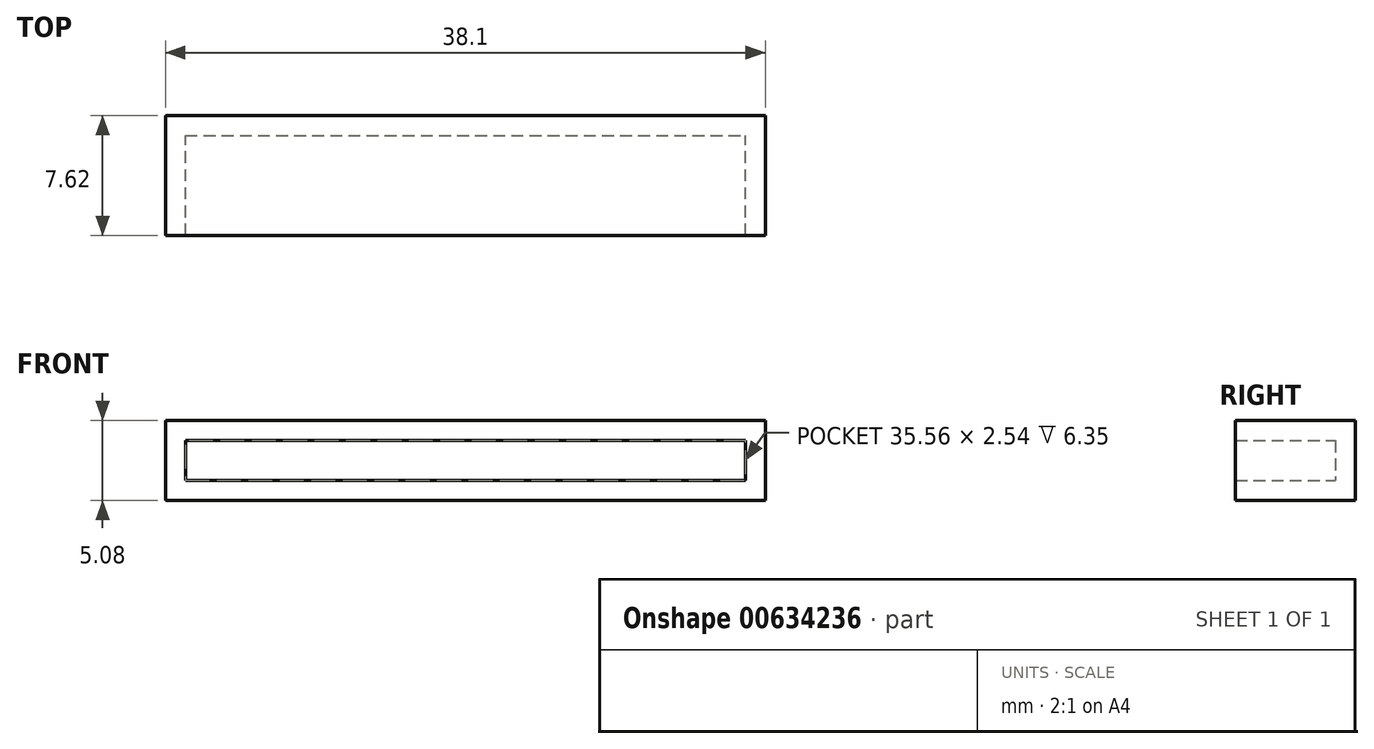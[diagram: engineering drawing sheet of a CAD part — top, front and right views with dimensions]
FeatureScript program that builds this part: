
annotation { "Feature Type Name" : "Feature", "Feature Type Description" : "" }
export const myFeature = defineFeature(function(context is Context, id is Id, definition is map)
    precondition{}
    {
        {
            var Q0;
            Q0=qCreatedBy(makeId("Front.planeOp"),FACE);
            var sketch = newSketch(context, id + "F0", { "sketchPlane" : qUnion([Q0])});
            skLineSegment(sketch, "E0.bottom", {"start": v(-65.34, 44.87) * mm, "end": v(-27.24, 44.87) * mm});
            skLineSegment(sketch, "E0.top", {"start": v(-65.34, 39.8) * mm, "end": v(-27.24, 39.8) * mm});
            skLineSegment(sketch, "E0.left", {"start": v(-65.34, 44.87) * mm, "end": v(-65.34, 39.8) * mm});
            skLineSegment(sketch, "E0.right", {"start": v(-27.24, 44.87) * mm, "end": v(-27.24, 39.8) * mm});
            skSolve(sketch);
        }
        {
            var Q0;
            Q0=makeQuery(id+"F0.imprint","IMPRINT",FACE,{"disambiguationData":[TD([[makeQuery(id+"F0.imprint","IMPRINT",EDGE,{"derivedFrom":sQuery(id+"F0.wireOp",EDGE,"E0.bottom")}),-1.0]])]});
            extrude(context, id + "F1", {"entities" : qUnion([Q0]), "depth" : 7.62 * mm, "offsetDistance" : 25.4 * mm});
        }
        {
            var Q0;
            Q0=makeQuery(id+"F1.opExtrude","CAP_FACE",FACE,{"disambiguationData":[OSD([sQuery(id+"F0.wireOp",EDGE,"E0.bottom"),sQuery(id+"F0.wireOp",EDGE,"E0.top"),sQuery(id+"F0.wireOp",EDGE,"E0.left"),sQuery(id+"F0.wireOp",EDGE,"E0.right")])],"isStart":false});
            shell(context, id + "F2", {"entities" : qUnion([Q0]), "thickness" : 2.54 * mm});
        }
        {
            var Q0;
            Q0=makeQuery(id+"F1.opExtrude","CAP_FACE",FACE,{"disambiguationData":[OSD([sQuery(id+"F0.wireOp",EDGE,"E0.bottom"),sQuery(id+"F0.wireOp",EDGE,"E0.top"),sQuery(id+"F0.wireOp",EDGE,"E0.left"),sQuery(id+"F0.wireOp",EDGE,"E0.right")])],"isStart":false});
            shell(context, id + "F3", {"entities" : qUnion([Q0]), "thickness" : 1.27 * mm});
        }
    });
